# Revit family: Deca_Acabamento de Descarga para Caixa Embutida_Deca You_4900.01
name_source: partatom
category: Plumbing Fixtures
units: mm (PartAtom-declared; Revit-internal decimal feet)

## family parameters
Cut with Voids When Loaded = No
Host = Face
Part Type = Normal
Room Calculation Point = No
Round Connector Dimension = Use Diameter
Shared = No

## types (8) — shared parameters
Acompanha o Produto = MÓDULO DE ACIONAMENTO MECÂNICO , TRAVAS E PARAFUSOS DE FIXAÇÃO
Aprovado por = quattroD
Atendimento ao Cliente = 0800 011 7073
Categoria = SISTEMAS DE DESCARGA
Composição Anel Vedação = -
Composição Assento = -
Composição Básica = Liga de Cobre (bronze e latão),Plásticos de Engenharia,Elastômeros
Composição Componente = -
Consumo = -
Cor Interna = -
Cor Secundária = -
Cores Componente = -
Criado por = quattroD
Código Pai = 4900.C01
Default Elevation = 1100 mm
Informações Complementares = -
Itens de Instalação = -
Linha = Deca You
Manufacturer = Deca
Norma = Não Possui
Peso Líquido (Kg) = 1.41
Pressão máx. funcionamento = -
Pressão mín. Aquec. Acúmulo = -
Pressão mín. Aquec. Passagem = -
Pressão mín. funcionamento = -
Saída de Esgoto = -
Segmento = -
Tipo de dispositivo economizador = -
Tipo de mecanismo utilizado = -
Tipo de rosca de entrada = -
Tipo de rosca de saída = -
URL = www.deca.com.br
Vazão na Pressão máx. (L/min) = -
Vazão na Pressão mín. (L/min) = -

## per-type parameters (varying)
| type | Cor Principal | Description | Material | Model |
| 4900.C01_Cromado | Cromado | Acabamento para Caixa Embutida - Cromado | Deca_Cromado | 4900.C01 |
| 4900.GF01.MT_Dark Antracite | Dark Antracite | Acabamento Caixa Embutida - Dark Antracite | Deca_Dark Antracite | 4900.GF01.MT |
| 4900.BL01.MT_Black Matte | Black Matte | Acabamento Caixa Embutida -Black Matte | Deca_Black Matte | 4900.BL01.MT |
| 4900.CT01.MT_Corten | Cortén | Acabamento Caixa Embutida - Corten | Deca_Corten | 4900.CT01.MT |
| 4900.INX01_Inox | Inox | Acabamento Caixa Embutida - Inox | Deca_Inox | 4900.INX01 |
| 4900.MR01.MT_Brown Matte | Brown Matte | Acabamento Caixa Embutida - Brown Matte | Deca_Brown Matte | 4900.MR01.MT |
| 4900.SM01.MT_Summer Gold | Summer Gold | Acabamento Caixa Embutida -Summer Gold | Deca_Summer Gold | 4900.SM01.MT |
| 4900.GL01.RD_Red Gold | Red Gold | Acabamento Caixa Embutida -Red Gold | Deca_Red Gold | 4900.GL01.RD |

## geometry (parser evidence)
native form markers: Sweep x2
no freeform markers — native parametric forms only
